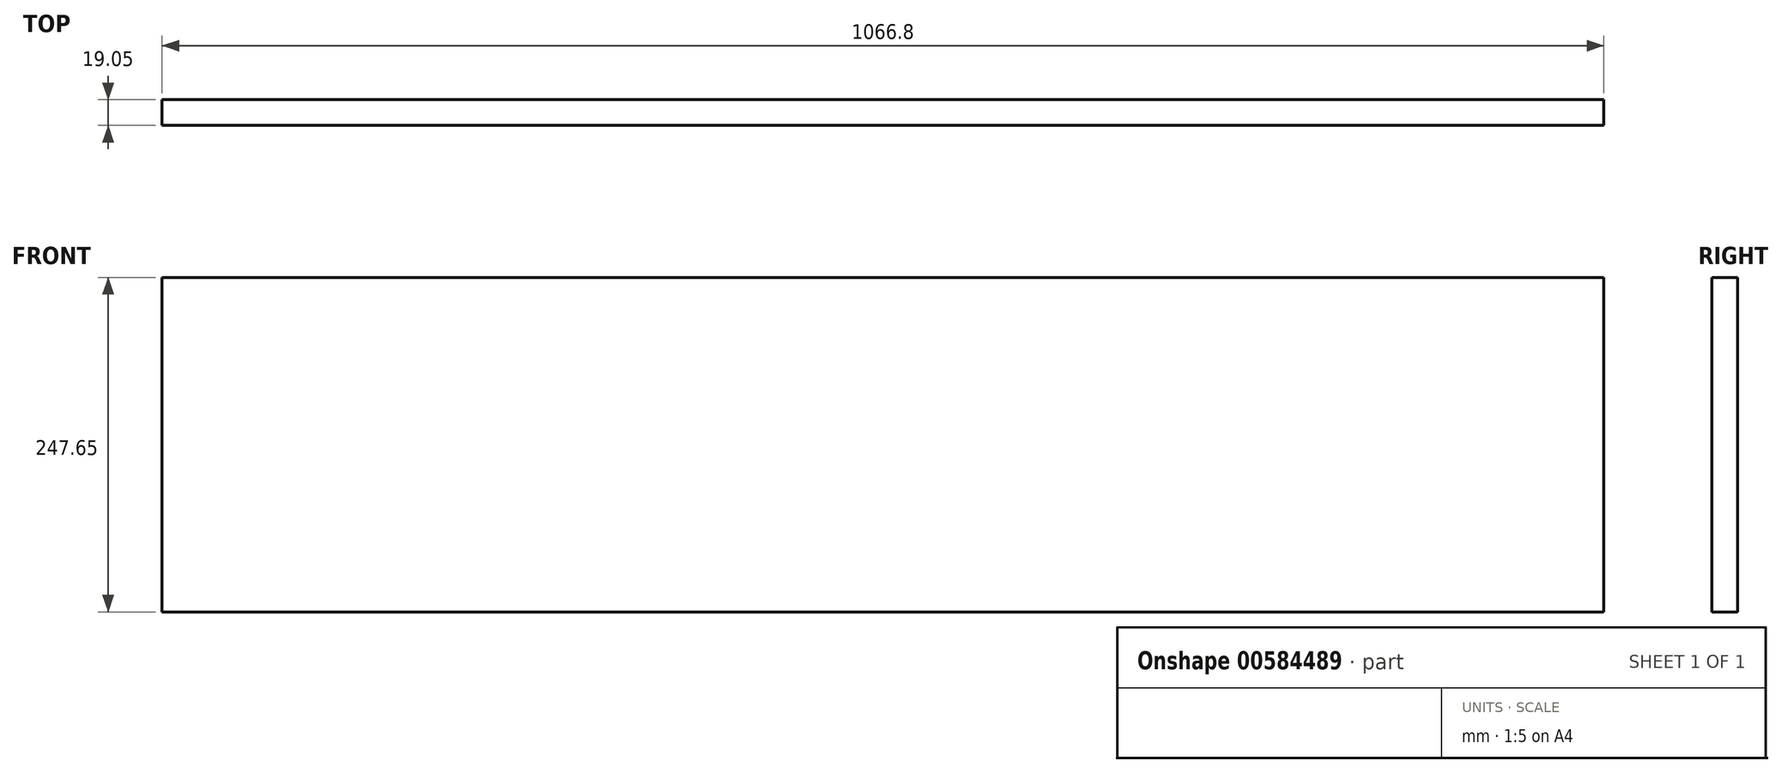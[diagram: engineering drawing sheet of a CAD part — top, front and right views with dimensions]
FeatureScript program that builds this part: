
annotation { "Feature Type Name" : "Feature", "Feature Type Description" : "" }
export const myFeature = defineFeature(function(context is Context, id is Id, definition is map)
    precondition{}
    {
        {
            var Q0;
            Q0=qCreatedBy(makeId("Front.planeOp"),FACE);
            var sketch = newSketch(context, id + "F0", { "sketchPlane" : qUnion([Q0])});
            skLineSegment(sketch, "E0.bottom", {"start": v(0, 0) * mm, "end": v(1066.8, 0) * mm});
            skLineSegment(sketch, "E0.top", {"start": v(0, 247.65) * mm, "end": v(1066.8, 247.65) * mm});
            skLineSegment(sketch, "E0.left", {"start": v(0, 0) * mm, "end": v(0, 247.65) * mm});
            skLineSegment(sketch, "E0.right", {"start": v(1066.8, 0) * mm, "end": v(1066.8, 247.65) * mm});
            skSolve(sketch);
        }
        {
            var Q0;
            Q0=makeQuery(id+"F0.imprint","IMPRINT",FACE,{"disambiguationData":[TD([[makeQuery(id+"F0.imprint","IMPRINT",EDGE,{"derivedFrom":sQuery(id+"F0.wireOp",EDGE,"E0.bottom")}),1.0]])]});
            extrude(context, id + "F1", {"entities" : qUnion([Q0]), "depth" : 19.05 * mm, "offsetDistance" : 25.4 * mm});
        }
    });
